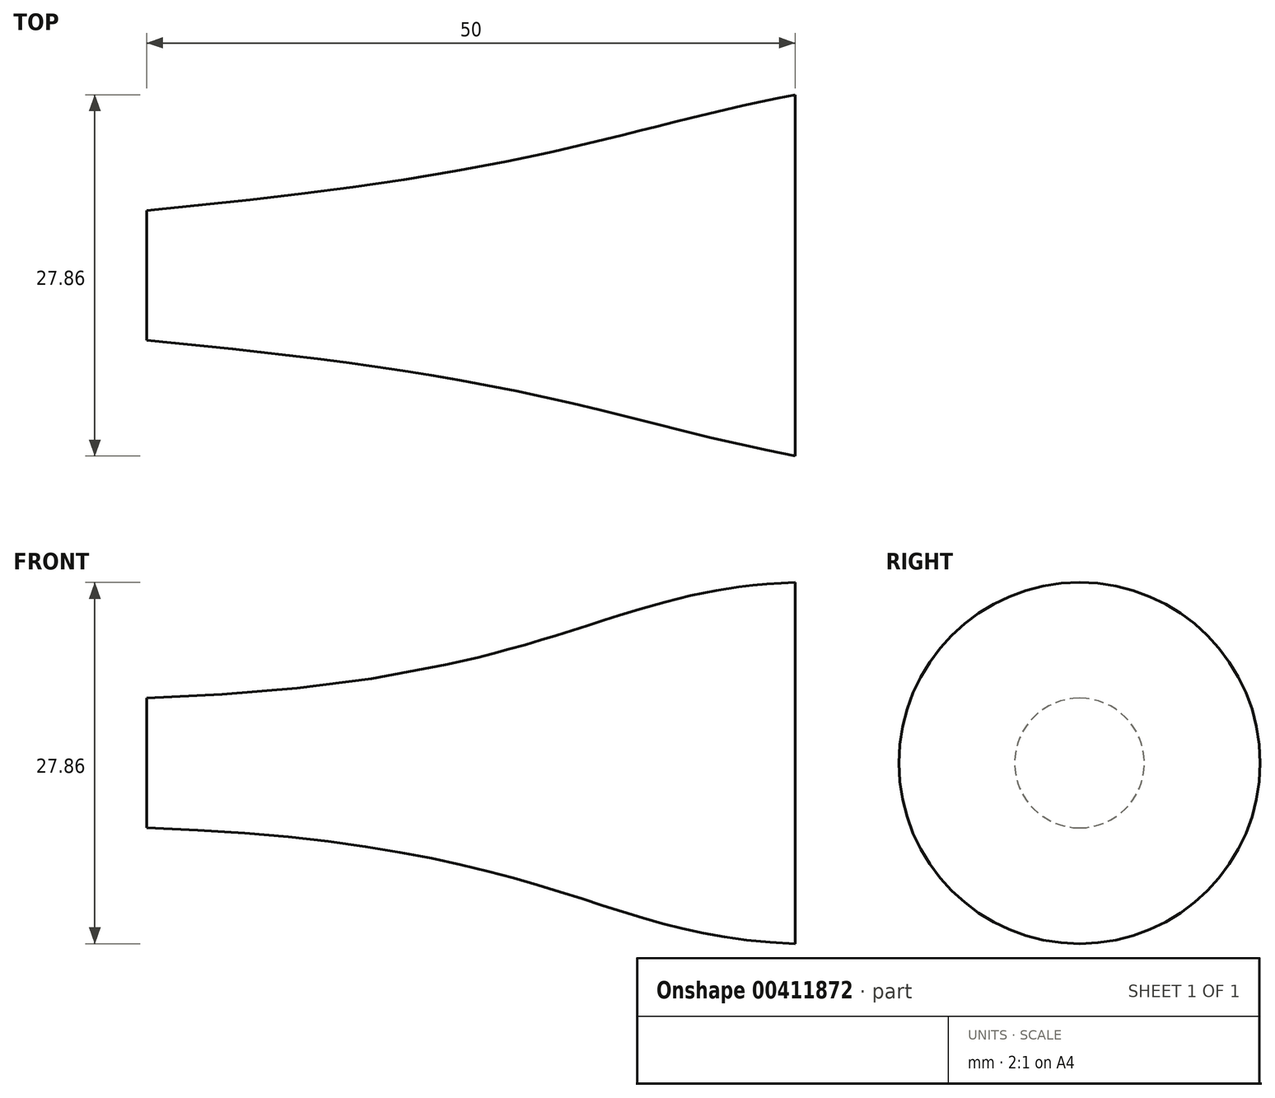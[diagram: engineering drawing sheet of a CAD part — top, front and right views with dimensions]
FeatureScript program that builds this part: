
annotation { "Feature Type Name" : "Feature", "Feature Type Description" : "" }
export const myFeature = defineFeature(function(context is Context, id is Id, definition is map)
    precondition{}
    {
        {
            var Q0;
            Q0=qCreatedBy(makeId("Right.planeOp"),FACE);
            var sketch = newSketch(context, id + "F0", { "sketchPlane" : qUnion([Q0])});
            skCircle(sketch, "E0", {"center": v(0, 0) * mm, "radius": 5 * mm});
            skPoint(sketch, "E1", {"position": v(0, 5) * mm});
            skPoint(sketch, "E2", {"position": v(0, -5) * mm});
            skSolve(sketch);
        }
        {
            var Q0;
            Q0=qCreatedBy(makeId("Right.planeOp"),FACE);
            cPlane(context, id + "F1", {"entities" : qUnion([Q0]), "cplaneType" : CPlaneType.OFFSET, "offset" : 50 * mm, "width" : 150 * mm, "height" : 150 * mm});
        }
        {
            var Q0;
            Q0=qCreatedBy(id+"F1.planeOp",FACE);
            var sketch = newSketch(context, id + "F2", { "sketchPlane" : qUnion([Q0])});
            skCircle(sketch, "E3", {"center": v(0, 0) * mm, "radius": 13.93 * mm});
            skPoint(sketch, "E4", {"position": v(0, 13.93) * mm});
            skPoint(sketch, "E5", {"position": v(0, -13.93) * mm});
            skSolve(sketch);
        }
        {
            var Q0;
            Q0=qCreatedBy(makeId("Front.planeOp"),FACE);
            var sketch = newSketch(context, id + "F3", { "sketchPlane" : qUnion([Q0])});
            skFitSpline(sketch, "E6", {"points": [v(0, 5) * mm, v(50, 13.93) * mm], "startDerivative": vector(93.87, 3.12) * mm, "endDerivative": vector(45.68, 1.44) * mm});
            skLineSegment(sketch, "E7", {"start": v(-1, 0) * mm, "end": v(51.25, 0) * mm, "construction": true});
            skFitSpline(sketch, "E8.MirrorCS", {"points": [v(0, -5) * mm, v(50, -13.93) * mm], "startDerivative": vector(93.87, -3.12) * mm, "endDerivative": vector(45.68, -1.44) * mm});
            skSolve(sketch);
        }
        {
            var Q0;
            Q0=makeQuery(id+"F0.imprint","IMPRINT",FACE,{"disambiguationData":[TD([[makeQuery(id+"F0.imprint","IMPRINT",EDGE,{"derivedFrom":sQuery(id+"F0.wireOp",EDGE,"E0")}),1.0]])]});
            var Q1;
            Q1=makeQuery(id+"F2.imprint","IMPRINT",FACE,{"disambiguationData":[TD([[makeQuery(id+"F2.imprint","IMPRINT",EDGE,{"derivedFrom":sQuery(id+"F2.wireOp",EDGE,"E3")}),1.0]])]});
            var Q2;
            Q2=sQuery(id+"F3.wireOp",EDGE,"E8.MirrorCS");
            var Q3;
            Q3=sQuery(id+"F3.wireOp",EDGE,"E6");
            loft(context, id + "F4", {"addGuides" : true, "sheetProfilesArray" : [{ "sheetProfileEntities" : qUnion([Q0]) }, { "sheetProfileEntities" : qUnion([Q1]) }], "guidesArray" : [{ "guideEntities" : qUnion([Q2]), "guideDerivativeType" : LoftGuideDerivativeType.DEFAULT, "guideDerivativeMagnitude" : 1 }, { "guideEntities" : qUnion([Q3]), "guideDerivativeType" : LoftGuideDerivativeType.DEFAULT, "guideDerivativeMagnitude" : 1 }]});
        }
    });
